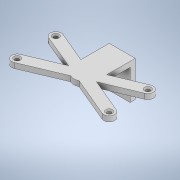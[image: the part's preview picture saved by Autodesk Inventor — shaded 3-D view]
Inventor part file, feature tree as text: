
AUTODESK INVENTOR PART (.ipt)
format: ipt  version: 2021 (Build 250183000, 183)  size: 197,120 bytes
history: native  units: mm
features: extrude x4, sketch x2, other x1, plane x1, chamfer x1
ambient origin geometry x8: Origin, YZ Plane, XZ Plane, XY Plane, X Axis, Y Axis, Z Axis, Center Point
bodies: Body1 (feature_tree)
feature tree (9):
  other  "HC-SR04.ipt"
  extrude  "Extrusion1"  Depth=10.0mm
  extrude  "Extrusion2"  Depth=5.0mm
  plane  "Arbeitsebene1"
  extrude  "Extrusion3"  Depth=5.0mm
  extrude  "Extrusion4"  Depth=5.0mm
  chamfer  "Fase1"  Distance=5.0mm
  sketch  "Skizze3"  dims[d0=10.0mm d1=1.8mm]
  sketch  "Skizze4"  dims[d3=8.0mm d5=5.0mm d6=5.0mm d7=5.0mm d8=5.0mm d9=5.0mm d10=5.0mm d11=5.0mm d12=5.0mm d13=3.0mm d14=12.0mm d15=8.0mm d16=2.4mm d17=2.4mm d18=0.0mm d19=14.0mm d20=0.0mm d21=2.4mm d22=0.0mm d23=0.0mm d25=18.439089mm d26=2.19513mm d27=5.446363mm d28=4.2mm d30=5.446363mm d31=12.0mm d32=0.0mm d33=0.6mm d34=2.0mm d35=45.0deg]
